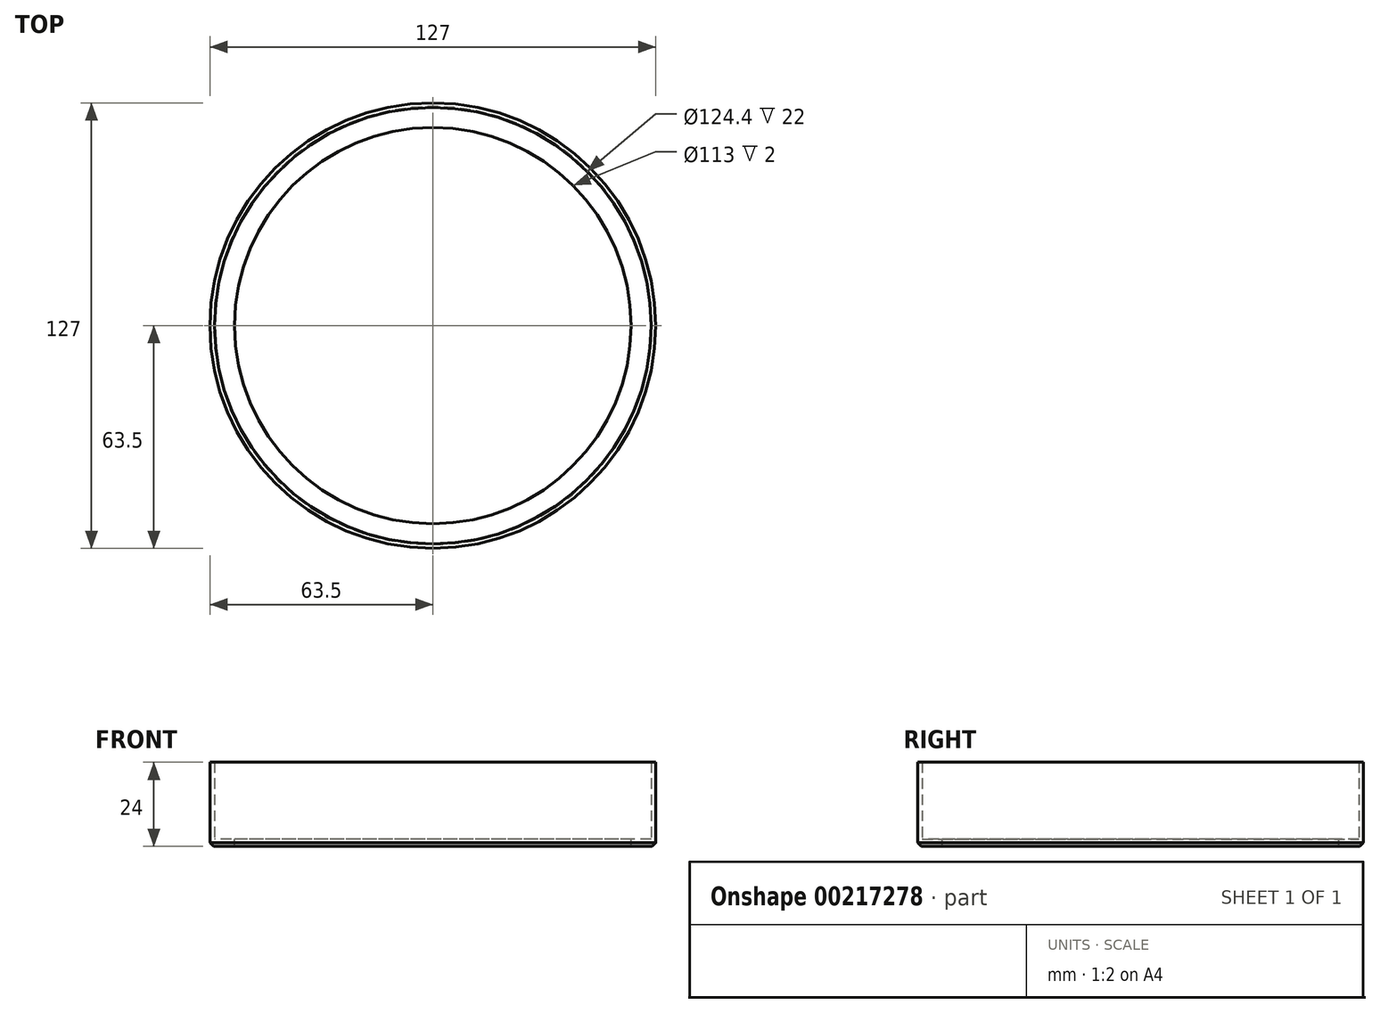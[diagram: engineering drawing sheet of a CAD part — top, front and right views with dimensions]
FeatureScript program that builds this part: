
annotation { "Feature Type Name" : "Feature", "Feature Type Description" : "" }
export const myFeature = defineFeature(function(context is Context, id is Id, definition is map)
    precondition{}
    {
        {
            var Q0;
            Q0=qCreatedBy(makeId("Top.planeOp"),FACE);
            var sketch = newSketch(context, id + "F0", { "sketchPlane" : qUnion([Q0])});
            skCircle(sketch, "E0", {"center": v(0, 0) * mm, "radius": 63.5 * mm});
            skCircle(sketch, "E1", {"center": v(0, 0) * mm, "radius": 62.2 * mm});
            skSolve(sketch);
        }
        {
            var Q0;
            Q0=qSketchRegion(id+"F0",true);
            extrude(context, id + "F1", {"entities" : qUnion([Q0]), "offsetDistance" : 25 * mm, "depth" : 22 * mm});
        }
        {
            var Q0;
            Q0=qCreatedBy(makeId("Top.planeOp"),FACE);
            var sketch = newSketch(context, id + "F2", { "sketchPlane" : qUnion([Q0])});
            skCircle(sketch, "E2", {"center": v(0, 0) * mm, "radius": 56.5 * mm});
            skCircle(sketch, "E3", {"center": v(0, 0) * mm, "radius": 63.5 * mm});
            skSolve(sketch);
        }
        {
            var Q0;
            Q0=qSketchRegion(id+"F2",true);
            extrude(context, id + "F3", {"entities" : qUnion([Q0]), "operationType" : NewBodyOperationType.ADD, "oppositeDirection" : true, "offsetDistance" : 25 * mm, "depth" : 2 * mm});
        }
        {
            var Q0;
            Q0=makeQuery(id+"F3.opExtrude","CAP_EDGE",EDGE,{"disambiguationData":[OSD([sQuery(id+"F2.wireOp",EDGE,"E3")])],"isStart":false});
            chamfer(context, id + "F4", {"entities" : qUnion([Q0]), "width" : 1 * mm, "tangentPropagation" : true});
        }
    });
